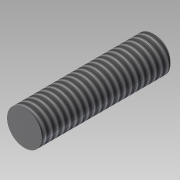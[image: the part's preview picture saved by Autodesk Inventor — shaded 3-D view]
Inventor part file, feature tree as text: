
AUTODESK INVENTOR PART (.ipt)
format: ipt  version: 2014 (Build 180170000, 170)  size: 87,552 bytes
history: native  units: mm
features: extrude x1, chamfer x1, thread x1, sketch x1
ambient origin geometry x8: Origin, YZ Plane, XZ Plane, XY Plane, X Axis, Y Axis, Z Axis, Center Point
bodies: Solid1 (feature_tree)
feature tree (4):
  extrude  "Extrusion1"  Depth=15.0mm TaperAngle=0.0deg
  chamfer  "Chamfer1"  Distance=2.0mm Angle=45.0deg
  thread  "Thread1"  [1 undecoded]
  sketch  "Sketch1"  dims[d0=4.0mm d1=15.0mm d2=0.0mm d3=0.3mm d4=2.0mm d5=45.0deg d6=10.0mm d7=0.0mm]
note: 1 required parameter value undecoded (feature->parameter linkage not recoverable at this tier; creation-order binding heuristic only, values carry confidence <= 0.55)
